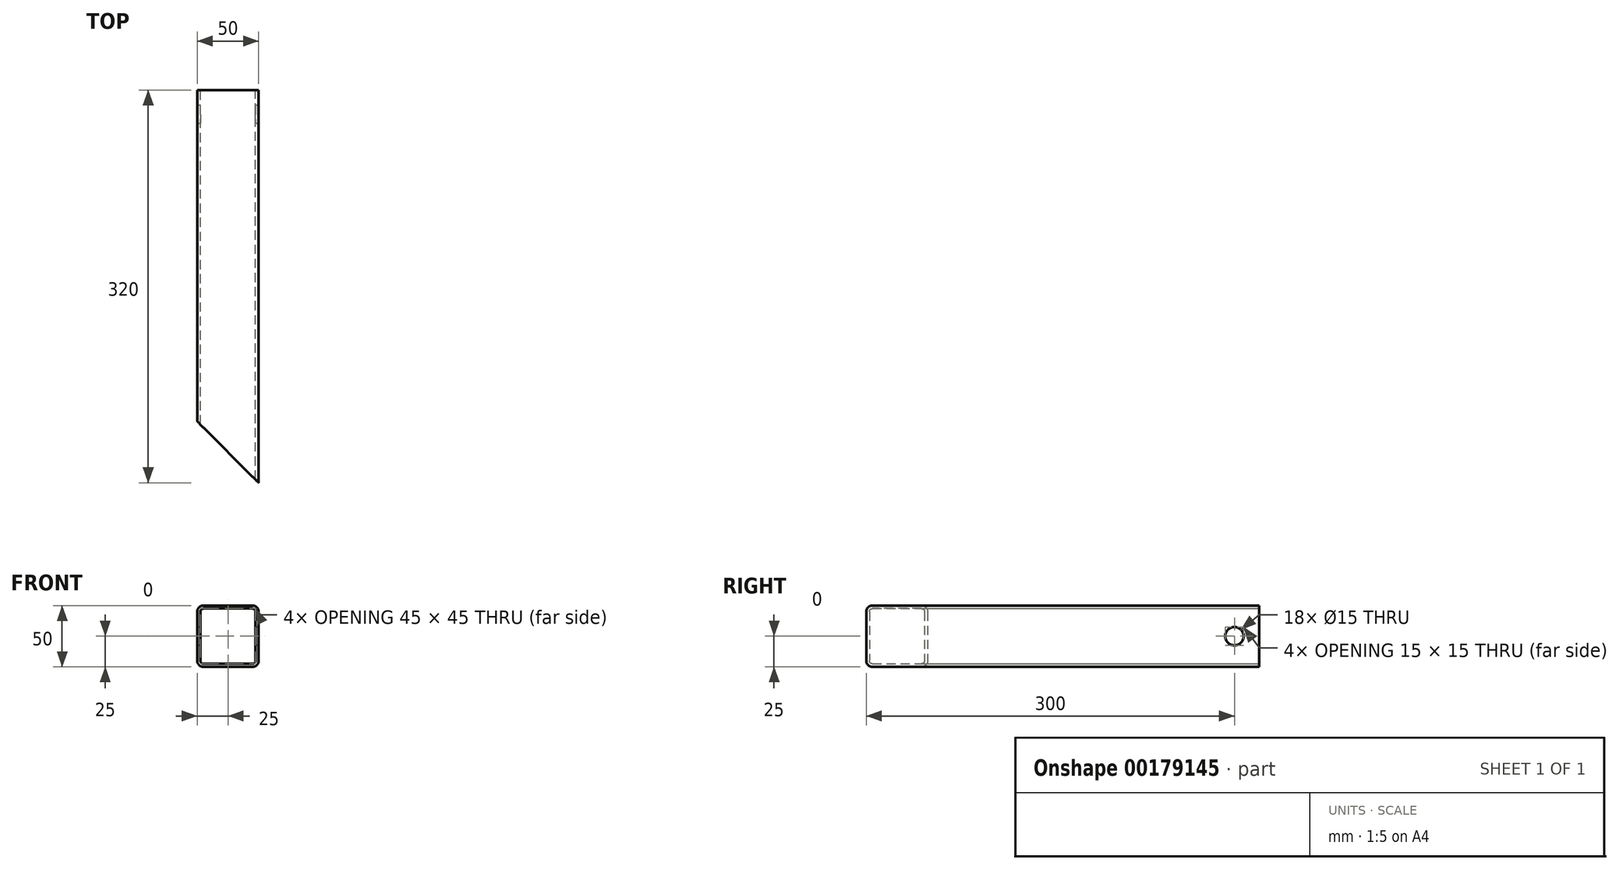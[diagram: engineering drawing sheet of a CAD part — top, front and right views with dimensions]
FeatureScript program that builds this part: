
annotation { "Feature Type Name" : "Feature", "Feature Type Description" : "" }
export const myFeature = defineFeature(function(context is Context, id is Id, definition is map)
    precondition{}
    {
        {
            var Q0;
            Q0=qCreatedBy(makeId("Front.planeOp"),FACE);
            var sketch = newSketch(context, id + "F0", { "sketchPlane" : qUnion([Q0])});
            skLineSegment(sketch, "E0.bottom", {"start": v(-25, 25) * mm, "end": v(25, 25) * mm});
            skLineSegment(sketch, "E0.top", {"start": v(-25, -25) * mm, "end": v(25, -25) * mm});
            skLineSegment(sketch, "E0.left", {"start": v(-25, 25) * mm, "end": v(-25, -25) * mm});
            skLineSegment(sketch, "E0.right", {"start": v(25, 25) * mm, "end": v(25, -25) * mm});
            skSolve(sketch);
        }
        {
            var Q0;
            Q0 = qSketchRegion(id + "F0", true);
            extrude(context, id + "F1", {"entities" : qUnion([Q0]), "depth" : 320 * mm});
        }
        {
            var Q0;
            Q0=makeQuery(id+"F1.opExtrude","SWEPT_FACE",FACE,{"disambiguationData":[OSD([sQuery(id+"F0.wireOp",EDGE,"E0.left")])]});
            var sketch = newSketch(context, id + "F2", { "sketchPlane" : qUnion([Q0])});
            skPoint(sketch, "E1", {"position": v(20, 0) * mm});
            skSolve(sketch);
        }
        {
            var Q0;
            Q0=makeQuery(id+"F1.opExtrude","SWEPT_FACE",FACE,{"disambiguationData":[OSD([sQuery(id+"F0.wireOp",EDGE,"E0.top")])]});
            var sketch = newSketch(context, id + "F3", { "sketchPlane" : qUnion([Q0])});
            skLineSegment(sketch, "E2", {"start": v(25, 320) * mm, "end": v(-25, 270) * mm});
            skLineSegment(sketch, "E3", {"start": v(-25, 270) * mm, "end": v(-25, 320) * mm});
            skLineSegment(sketch, "E4", {"start": v(-25, 320) * mm, "end": v(25, 320) * mm});
            skSolve(sketch);
        }
        {
            var Q0;
            Q0=makeQuery(id+"F3.imprint","IMPRINT",FACE,{"disambiguationData":[TD([[makeQuery(id+"F3.imprint","IMPRINT",EDGE,{"derivedFrom":sQuery(id+"F3.wireOp",EDGE,"E2")}),-1.0]])]});
            extrude(context, id + "F4", {"entities" : qUnion([Q0]), "operationType" : NewBodyOperationType.REMOVE, "oppositeDirection" : true, "depth" : 74.4 * mm});
        }
        {
            var Q0;
            Q0=makeQuery(id+"F1.opExtrude","SWEPT_EDGE",EDGE,{"disambiguationData":[OSD([sQuery(id+"F0.wireOp",EDGE,"E0.bottom"),sQuery(id+"F0.wireOp",EDGE,"E0.right")])]});
            var Q1;
            Q1=makeQuery(id+"F1.opExtrude","SWEPT_EDGE",EDGE,{"disambiguationData":[OSD([sQuery(id+"F0.wireOp",EDGE,"E0.bottom"),sQuery(id+"F0.wireOp",EDGE,"E0.left")])]});
            var Q2;
            Q2=makeQuery(id+"F1.opExtrude","SWEPT_EDGE",EDGE,{"disambiguationData":[OSD([sQuery(id+"F0.wireOp",EDGE,"E0.top"),sQuery(id+"F0.wireOp",EDGE,"E0.left")])]});
            var Q3;
            Q3=makeQuery(id+"F1.opExtrude","SWEPT_EDGE",EDGE,{"disambiguationData":[OSD([sQuery(id+"F0.wireOp",EDGE,"E0.top"),sQuery(id+"F0.wireOp",EDGE,"E0.right")])]});
            fillet(context, id + "F5", {"entities" : qUnion([Q0, Q1, Q2, Q3]), "radius" : 5 * mm, "tangentPropagation" : true, "allowEdgeOverflow" : false});
        }
        {
            var Q0;
            Q0=makeQuery(id+"F1.opExtrude","CAP_FACE",FACE,{"disambiguationData":[OSD([sQuery(id+"F0.wireOp",EDGE,"E0.bottom"),sQuery(id+"F0.wireOp",EDGE,"E0.top"),sQuery(id+"F0.wireOp",EDGE,"E0.left"),sQuery(id+"F0.wireOp",EDGE,"E0.right")])],"isStart":false});
            var Q1;
            Q1=makeQuery(id+"F1.opExtrude","CAP_FACE",FACE,{"disambiguationData":[OSD([sQuery(id+"F0.wireOp",EDGE,"E0.bottom"),sQuery(id+"F0.wireOp",EDGE,"E0.top"),sQuery(id+"F0.wireOp",EDGE,"E0.left"),sQuery(id+"F0.wireOp",EDGE,"E0.right")])],"isStart":true});
            var Q2;
            Q2=makeQuery(id+"F4.boolean.opBoolean","COPY",FACE,{"derivedFrom":makeQuery(id+"F4.opExtrude","SWEPT_FACE",FACE,{"disambiguationData":[OSD([sQuery(id+"F3.wireOp",EDGE,"E2")])]})});
            shell(context, id + "F6", {"entities" : qUnion([Q0, Q1, Q2]), "thickness" : 2.5 * mm});
        }
        {
            var Q0;
            Q0=sQuery(id+"F2.wireOp",VERTEX,"E1");
            var Q1;
            Q1=makeQuery(id+"F1.opExtrude","SWEPT_BODY",BODY,{"disambiguationData":[OSD([sQuery(id+"F0.wireOp",EDGE,"E0.bottom"),sQuery(id+"F0.wireOp",EDGE,"E0.top"),sQuery(id+"F0.wireOp",EDGE,"E0.left"),sQuery(id+"F0.wireOp",EDGE,"E0.right")])]});
            hole(context, id + "F7", {"style" : HoleStyle.SIMPLE, "endStyle" : HoleEndStyle.THROUGH, "holeDiameter" : 15 * mm, "locations" : qUnion([Q0]), "scope" : qUnion([Q1]), "isTappedThrough" : true});
        }
    });
